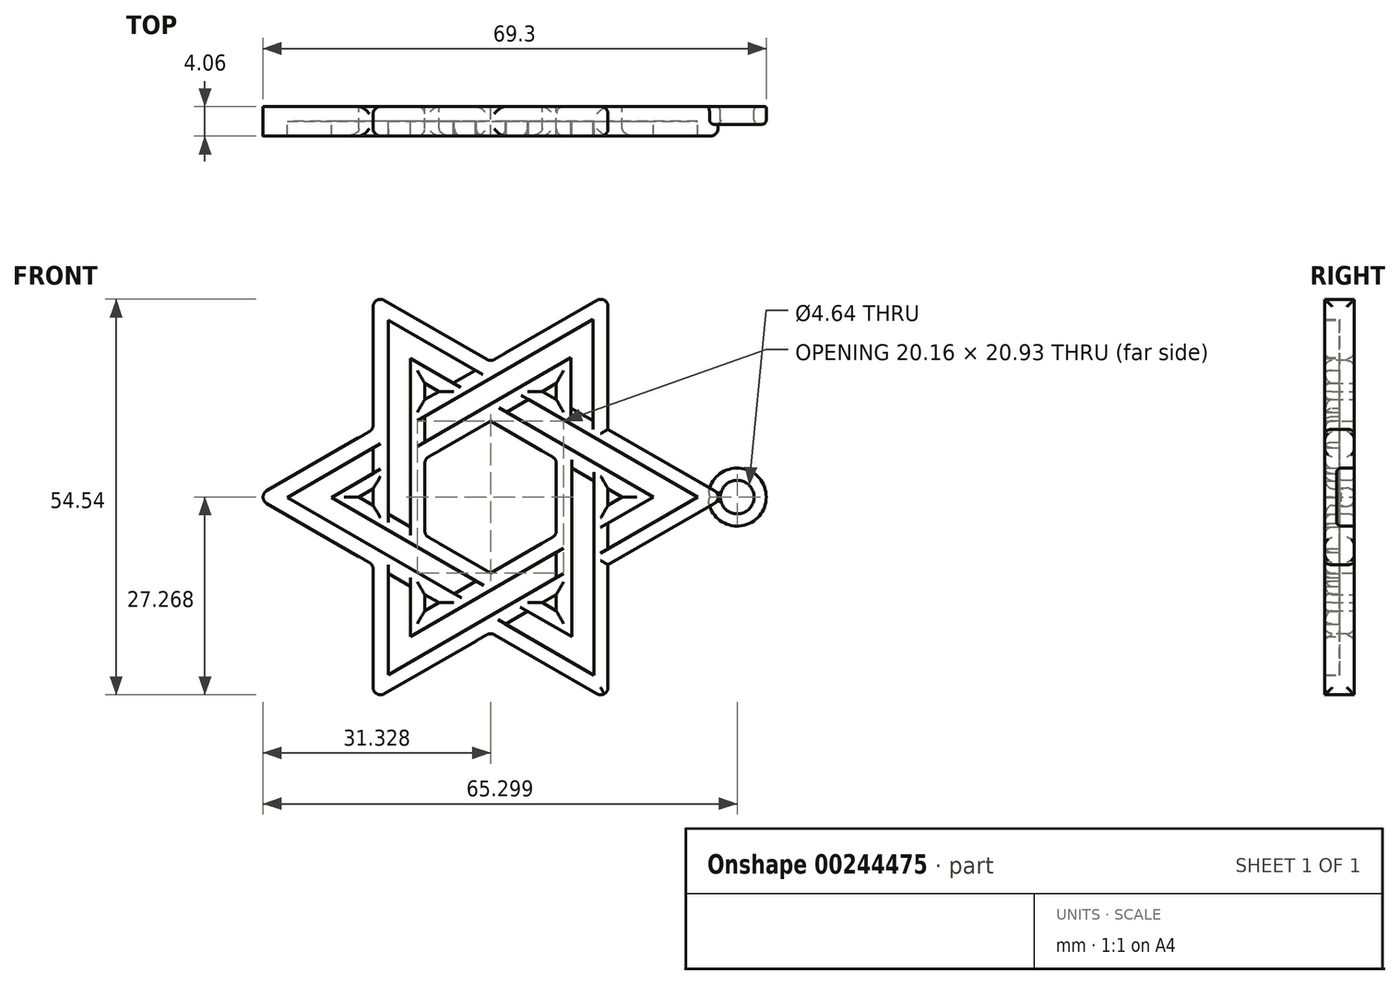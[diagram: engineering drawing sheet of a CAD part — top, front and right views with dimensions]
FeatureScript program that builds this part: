
annotation { "Feature Type Name" : "Feature", "Feature Type Description" : "" }
export const myFeature = defineFeature(function(context is Context, id is Id, definition is map)
    precondition{}
    {
        {
            var Q0;
            Q0=qCreatedBy(makeId("Front.planeOp"),FACE);
            var sketch = newSketch(context, id + "F0", { "sketchPlane" : qUnion([Q0])});
            skLineSegment(sketch, "E0.0", {"start": v(-25.14, 72.22) * mm, "end": v(-25.14, 48.87) * mm});
            skLineSegment(sketch, "E0.1", {"start": v(-25.14, 2.18) * mm, "end": v(-45.36, 13.85) * mm});
            skLineSegment(sketch, "E0.2", {"start": v(-85.8, 37.2) * mm, "end": v(-65.58, 48.87) * mm});
            skPoint(sketch, "E0.0.midPoint", {"position": v(-25.14, 37.2) * mm});
            skCircle(sketch, "E1.cCircle", {"center": v(-45.36, 37.2) * mm, "radius": 20.22 * mm, "construction": true});
            skLineSegment(sketch, "E1.0", {"start": v(-65.58, 2.18) * mm, "end": v(-65.58, 25.53) * mm});
            skLineSegment(sketch, "E1.1", {"start": v(-65.58, 72.22) * mm, "end": v(-45.36, 60.54) * mm});
            skLineSegment(sketch, "E1.2", {"start": v(-4.93, 37.2) * mm, "end": v(-25.14, 25.53) * mm});
            skPoint(sketch, "E1.0.midPoint", {"position": v(-65.58, 37.2) * mm});
            skLineSegment(sketch, "E2", {"start": v(-36.47, 55.41) * mm, "end": v(-25.14, 48.87) * mm});
            skLineSegment(sketch, "E3", {"start": v(-45.36, 60.54) * mm, "end": v(-25.14, 72.22) * mm});
            skLineSegment(sketch, "E4", {"start": v(-25.14, 48.87) * mm, "end": v(-4.93, 37.2) * mm});
            skLineSegment(sketch, "E5", {"start": v(-25.14, 38.6) * mm, "end": v(-25.14, 25.53) * mm});
            skLineSegment(sketch, "E6", {"start": v(-25.14, 25.53) * mm, "end": v(-25.14, 2.18) * mm});
            skLineSegment(sketch, "E7", {"start": v(-34.03, 20.4) * mm, "end": v(-45.36, 13.85) * mm});
            skLineSegment(sketch, "E8", {"start": v(-45.36, 13.85) * mm, "end": v(-65.58, 2.18) * mm});
            skLineSegment(sketch, "E9", {"start": v(-54.25, 18.99) * mm, "end": v(-65.58, 25.53) * mm});
            skLineSegment(sketch, "E10", {"start": v(-65.58, 25.53) * mm, "end": v(-85.8, 37.2) * mm});
            skLineSegment(sketch, "E11", {"start": v(-65.58, 35.8) * mm, "end": v(-65.58, 48.87) * mm});
            skLineSegment(sketch, "E12", {"start": v(-65.58, 48.87) * mm, "end": v(-65.58, 72.22) * mm});
            skLineSegment(sketch, "E13", {"start": v(-56.69, 54) * mm, "end": v(-45.36, 60.54) * mm});
            skLineSegment(sketch, "E14.0", {"start": v(-56.69, 30.66) * mm, "end": v(-56.69, 43.74) * mm});
            skLineSegment(sketch, "E14.1", {"start": v(-45.36, 50.28) * mm, "end": v(-34.03, 43.74) * mm});
            skLineSegment(sketch, "E14.2", {"start": v(-34.03, 43.74) * mm, "end": v(-34.03, 30.66) * mm});
            skLineSegment(sketch, "E14.3", {"start": v(-56.69, 43.74) * mm, "end": v(-45.36, 50.28) * mm});
            skLineSegment(sketch, "E14.4", {"start": v(-34.03, 30.66) * mm, "end": v(-45.36, 24.12) * mm});
            skLineSegment(sketch, "E14.5", {"start": v(-45.36, 24.12) * mm, "end": v(-56.69, 30.66) * mm});
            skLineSegment(sketch, "E15", {"start": v(-54.2, 55.38) * mm, "end": v(-56.69, 56.82) * mm});
            skLineSegment(sketch, "E16", {"start": v(-56.69, 43.74) * mm, "end": v(-56.69, 56.82) * mm});
            skLineSegment(sketch, "E17", {"start": v(-34.03, 43.74) * mm, "end": v(-22.7, 37.2) * mm});
            skLineSegment(sketch, "E18", {"start": v(-25.2, 35.76) * mm, "end": v(-22.7, 37.2) * mm});
            skLineSegment(sketch, "E19", {"start": v(-65.53, 38.64) * mm, "end": v(-68.01, 37.2) * mm});
            skLineSegment(sketch, "E20", {"start": v(-56.69, 30.66) * mm, "end": v(-68.01, 37.2) * mm});
            skLineSegment(sketch, "E21", {"start": v(-56.69, 20.45) * mm, "end": v(-56.69, 17.58) * mm});
            skLineSegment(sketch, "E22", {"start": v(-45.36, 24.12) * mm, "end": v(-56.69, 17.58) * mm});
            skLineSegment(sketch, "E23", {"start": v(-36.52, 19.02) * mm, "end": v(-34.03, 17.58) * mm});
            skLineSegment(sketch, "E24", {"start": v(-34.03, 30.66) * mm, "end": v(-34.03, 17.58) * mm});
            skLineSegment(sketch, "E25", {"start": v(-45.36, 50.28) * mm, "end": v(-34.03, 56.82) * mm});
            skLineSegment(sketch, "E26", {"start": v(-34.03, 53.94) * mm, "end": v(-34.03, 56.82) * mm});
            skPoint(sketch, "E27.orphan", {"position": v(-30.1, 59.09) * mm});
            skPoint(sketch, "E28.orphan", {"position": v(-60.62, 59.09) * mm});
            skLineSegment(sketch, "E29.0", {"start": v(-44.1, 58.34) * mm, "end": v(-27.68, 67.82) * mm});
            skLineSegment(sketch, "E29.1", {"start": v(-56.69, 51.07) * mm, "end": v(-44.1, 58.34) * mm});
            skLineSegment(sketch, "E30.0", {"start": v(-46.63, 52.48) * mm, "end": v(-31.5, 61.22) * mm});
            skLineSegment(sketch, "E31.0", {"start": v(-31.5, 52.54) * mm, "end": v(-31.5, 61.22) * mm});
            skLineSegment(sketch, "E32.trimOffspring", {"start": v(-27.68, 67.82) * mm, "end": v(-27.68, 50.34) * mm});
            skLineSegment(sketch, "E33.trimOffspring", {"start": v(-54.15, 55.4) * mm, "end": v(-54.15, 55.47) * mm});
            skLineSegment(sketch, "E34.trimOffspring", {"start": v(-56.69, 46.67) * mm, "end": v(-46.63, 52.48) * mm});
            skLineSegment(sketch, "E35.0", {"start": v(-46.57, 16.05) * mm, "end": v(-62.98, 6.58) * mm});
            skLineSegment(sketch, "E35.1", {"start": v(-34.03, 23.29) * mm, "end": v(-46.57, 16.05) * mm});
            skLineSegment(sketch, "E36.0", {"start": v(-44.03, 21.92) * mm, "end": v(-59.17, 13.18) * mm});
            skLineSegment(sketch, "E37.0", {"start": v(-59.17, 21.83) * mm, "end": v(-59.17, 13.18) * mm});
            skLineSegment(sketch, "E38.trimOffspring", {"start": v(-62.98, 6.58) * mm, "end": v(-62.98, 24.03) * mm});
            skLineSegment(sketch, "E39.trimOffspring", {"start": v(-34.03, 27.69) * mm, "end": v(-44.03, 21.92) * mm});
            skLineSegment(sketch, "E40.0", {"start": v(-27.55, 25.45) * mm, "end": v(-27.55, 6.5) * mm});
            skLineSegment(sketch, "E41.0", {"start": v(-31.36, 30.59) * mm, "end": v(-31.36, 13.1) * mm});
            skLineSegment(sketch, "E42.0", {"start": v(-39, 17.52) * mm, "end": v(-31.36, 13.1) * mm});
            skLineSegment(sketch, "E43.trimOffspring", {"start": v(-27.55, 6.5) * mm, "end": v(-42.81, 15.32) * mm});
            skLineSegment(sketch, "E44.trimOffspring", {"start": v(-31.36, 42.2) * mm, "end": v(-31.36, 30.59) * mm});
            skLineSegment(sketch, "E45.0", {"start": v(-62.93, 48.75) * mm, "end": v(-62.93, 67.7) * mm});
            skLineSegment(sketch, "E45.1", {"start": v(-62.93, 34.26) * mm, "end": v(-62.93, 48.75) * mm});
            skLineSegment(sketch, "E46.0", {"start": v(-59.12, 43.62) * mm, "end": v(-59.12, 61.1) * mm});
            skLineSegment(sketch, "E47.0", {"start": v(-51.76, 56.85) * mm, "end": v(-59.12, 61.1) * mm});
            skLineSegment(sketch, "E48.trimOffspring", {"start": v(-62.93, 67.7) * mm, "end": v(-47.95, 59.05) * mm});
            skLineSegment(sketch, "E49.trimOffspring", {"start": v(-59.12, 32.06) * mm, "end": v(-59.12, 43.62) * mm});
            skLineSegment(sketch, "E50", {"start": v(-27.55, 25.45) * mm, "end": v(-27.55, 40) * mm});
            skLineSegment(sketch, "E51.0", {"start": v(-63.96, 27.67) * mm, "end": v(-80.37, 37.15) * mm});
            skLineSegment(sketch, "E52.0", {"start": v(-57.6, 28.4) * mm, "end": v(-72.75, 37.15) * mm});
            skLineSegment(sketch, "E53.0", {"start": v(-65.58, 41.28) * mm, "end": v(-72.75, 37.15) * mm});
            skLineSegment(sketch, "E54.trimOffspring", {"start": v(-80.37, 37.15) * mm, "end": v(-65.58, 45.68) * mm});
            skLineSegment(sketch, "E55.trimOffspring", {"start": v(-47.77, 22.73) * mm, "end": v(-57.6, 28.4) * mm});
            skLineSegment(sketch, "E56.0", {"start": v(-26.1, 46.67) * mm, "end": v(-9.68, 37.2) * mm});
            skLineSegment(sketch, "E56.1", {"start": v(-38.85, 54.04) * mm, "end": v(-26.1, 46.67) * mm});
            skLineSegment(sketch, "E57.0", {"start": v(-32.44, 45.94) * mm, "end": v(-17.3, 37.2) * mm});
            skLineSegment(sketch, "E58.0", {"start": v(-25.14, 32.67) * mm, "end": v(-17.3, 37.2) * mm});
            skLineSegment(sketch, "E59.trimOffspring", {"start": v(-9.68, 37.2) * mm, "end": v(-25.14, 28.27) * mm});
            skLineSegment(sketch, "E60.trimOffspring", {"start": v(-42.66, 51.84) * mm, "end": v(-32.44, 45.94) * mm});
            skLineSegment(sketch, "E61", {"start": v(-63.96, 27.67) * mm, "end": v(-51.58, 20.53) * mm});
            skSolve(sketch);
        }
        {
            var Q0;
            Q0 = qSketchRegion(id + "F0", true);
            var Q1;
            {var subQ7=sQuery(id+"F0.wireOp",EDGE,"E14.1");Q1=makeQuery(id+"F0.imprint","IMPRINT",FACE,{"disambiguationData":[TD([[makeQuery(id+"F0.imprint","IMPRINT",EDGE,{"derivedFrom":subQ7}),1.0]])]});}
            var Q2;
            {var subQ10=sQuery(id+"F0.wireOp",EDGE,"E14.3");Q2=makeQuery(id+"F0.imprint","IMPRINT",FACE,{"disambiguationData":[TD([[makeQuery(id+"F0.imprint","IMPRINT",EDGE,{"derivedFrom":subQ10}),1.0]])]});}
            var Q3;
            {var subQ9=sQuery(id+"F0.wireOp",EDGE,"E14.2");Q3=makeQuery(id+"F0.imprint","IMPRINT",FACE,{"disambiguationData":[TD([[makeQuery(id+"F0.imprint","IMPRINT",EDGE,{"derivedFrom":subQ9}),1.0]])]});}
            var Q4;
            {var subQ10=sQuery(id+"F0.wireOp",EDGE,"E14.4");Q4=makeQuery(id+"F0.imprint","IMPRINT",FACE,{"disambiguationData":[TD([[makeQuery(id+"F0.imprint","IMPRINT",EDGE,{"derivedFrom":subQ10}),1.0]])]});}
            var Q5;
            {var subQ7=sQuery(id+"F0.wireOp",EDGE,"E14.5");Q5=makeQuery(id+"F0.imprint","IMPRINT",FACE,{"disambiguationData":[TD([[makeQuery(id+"F0.imprint","IMPRINT",EDGE,{"derivedFrom":subQ7}),1.0]])]});}
            var Q6;
            {var subQ7=sQuery(id+"F0.wireOp",EDGE,"E14.0");Q6=makeQuery(id+"F0.imprint","IMPRINT",FACE,{"disambiguationData":[TD([[makeQuery(id+"F0.imprint","IMPRINT",EDGE,{"derivedFrom":subQ7}),1.0]])]});}
            extrude(context, id + "F1", {"entities" : qUnion([Q0, Q1, Q2, Q3, Q4, Q5, Q6]), "depth" : 5.08 * mm});
        }
        {
            var Q0;
            Q0=makeQuery(id+"F0.imprint","IMPRINT",FACE,{"disambiguationData":[TD([[makeQuery(id+"F0.imprint","IMPRINT",EDGE,{"derivedFrom":sQuery(id+"F0.wireOp",EDGE,"E45.0")}),-1.0]])]});
            var Q1;
            Q1=makeQuery(id+"F0.imprint","IMPRINT",FACE,{"disambiguationData":[TD([[makeQuery(id+"F0.imprint","IMPRINT",EDGE,{"derivedFrom":sQuery(id+"F0.wireOp",EDGE,"E29.0")}),-1.0]])]});
            var Q2;
            Q2=makeQuery(id+"F0.imprint","IMPRINT",FACE,{"disambiguationData":[TD([[makeQuery(id+"F0.imprint","IMPRINT",EDGE,{"derivedFrom":sQuery(id+"F0.wireOp",EDGE,"E56.0")}),-1.0]])]});
            var Q3;
            Q3=makeQuery(id+"F0.imprint","IMPRINT",FACE,{"disambiguationData":[TD([[makeQuery(id+"F0.imprint","IMPRINT",EDGE,{"derivedFrom":sQuery(id+"F0.wireOp",EDGE,"E40.0")}),-1.0]])]});
            var Q4;
            Q4=makeQuery(id+"F0.imprint","IMPRINT",FACE,{"disambiguationData":[TD([[makeQuery(id+"F0.imprint","IMPRINT",EDGE,{"derivedFrom":sQuery(id+"F0.wireOp",EDGE,"E35.0")}),-1.0]])]});
            var Q5;
            Q5=makeQuery(id+"F0.imprint","IMPRINT",FACE,{"disambiguationData":[TD([[makeQuery(id+"F0.imprint","IMPRINT",EDGE,{"derivedFrom":sQuery(id+"F0.wireOp",EDGE,"E51.0")}),-1.0]])]});
            extrude(context, id + "F2", {"entities" : qUnion([Q0, Q1, Q2, Q3, Q4, Q5]), "operationType" : NewBodyOperationType.ADD, "depth" : 2.54 * mm});
        }
        {
            var Q0;
            {var subQ0=sQuery(id+"F0.wireOp",EDGE,"3791ea46-a5e9-4ab1-a861-55320faec565.trimOffspring");var subQ1=sQuery(id+"F0.wireOp",EDGE,"E60.trimOffspring");var subQ2=sQuery(id+"F0.wireOp",EDGE,"E59.trimOffspring");var subQ3=sQuery(id+"F0.wireOp",EDGE,"b85427f2-48fe-4ba3-bfe0-d898cf596bcf.0");var subQ4=sQuery(id+"F0.wireOp",EDGE,"E58.0");var subQ5=sQuery(id+"F0.wireOp",EDGE,"E57.0");var subQ6=sQuery(id+"F0.wireOp",EDGE,"E56.1");var subQ7=sQuery(id+"F0.wireOp",EDGE,"E56.0");var subQ8=sQuery(id+"F0.wireOp",EDGE,"E61");var subQ9=sQuery(id+"F0.wireOp",EDGE,"51e37403-e772-4eac-ae45-40e6eff04354.trimOffspring");var subQ10=sQuery(id+"F0.wireOp",EDGE,"E55.trimOffspring");var subQ11=sQuery(id+"F0.wireOp",EDGE,"E54.trimOffspring");var subQ12=sQuery(id+"F0.wireOp",EDGE,"bc42f384-2414-4325-8679-d2749f00dfbf.0");var subQ13=sQuery(id+"F0.wireOp",EDGE,"E53.0");var subQ14=sQuery(id+"F0.wireOp",EDGE,"E52.0");var subQ15=sQuery(id+"F0.wireOp",EDGE,"E51.0");var subQ16=sQuery(id+"F0.wireOp",EDGE,"242a467f-4fe9-4b40-a065-2ee8d1ec2a3d.trimOffspring");var subQ17=sQuery(id+"F0.wireOp",EDGE,"E49.trimOffspring");var subQ18=sQuery(id+"F0.wireOp",EDGE,"E48.trimOffspring");var subQ19=sQuery(id+"F0.wireOp",EDGE,"76f297ee-8d65-411f-9fbc-2a5ef9db8cba.0");var subQ20=sQuery(id+"F0.wireOp",EDGE,"E47.0");var subQ21=sQuery(id+"F0.wireOp",EDGE,"E46.0");var subQ22=sQuery(id+"F0.wireOp",EDGE,"E45.1");var subQ23=sQuery(id+"F0.wireOp",EDGE,"E45.0");var subQ24=sQuery(id+"F0.wireOp",EDGE,"E50");var subQ25=sQuery(id+"F0.wireOp",EDGE,"70ba2939-24bf-49fa-9c79-4e4c6b037132.trimOffspring");var subQ26=sQuery(id+"F0.wireOp",EDGE,"E44.trimOffspring");var subQ27=sQuery(id+"F0.wireOp",EDGE,"E43.trimOffspring");var subQ28=sQuery(id+"F0.wireOp",EDGE,"54159dc6-59ae-437a-bbb7-fb0cfa8d277d.0");var subQ29=sQuery(id+"F0.wireOp",EDGE,"E42.0");var subQ30=sQuery(id+"F0.wireOp",EDGE,"E41.0");var subQ31=sQuery(id+"F0.wireOp",EDGE,"E40.0");var subQ32=sQuery(id+"F0.wireOp",EDGE,"9e70e6bb-2b84-45bd-9e91-4ec9be9ea51e.trimOffspring");var subQ33=sQuery(id+"F0.wireOp",EDGE,"E39.trimOffspring");var subQ34=sQuery(id+"F0.wireOp",EDGE,"E38.trimOffspring");var subQ35=sQuery(id+"F0.wireOp",EDGE,"b6243921-ca12-479c-9c0a-cf2d943f5022.0");var subQ36=sQuery(id+"F0.wireOp",EDGE,"E37.0");var subQ37=sQuery(id+"F0.wireOp",EDGE,"E36.0");var subQ38=sQuery(id+"F0.wireOp",EDGE,"E35.1");var subQ39=sQuery(id+"F0.wireOp",EDGE,"E35.0");var subQ40=sQuery(id+"F0.wireOp",EDGE,"5713abb0-698d-4ae2-b673-d070041138cb.trimOffspring");var subQ41=sQuery(id+"F0.wireOp",EDGE,"E34.trimOffspring");var subQ42=sQuery(id+"F0.wireOp",EDGE,"E32.trimOffspring");var subQ43=sQuery(id+"F0.wireOp",EDGE,"0343537c-8046-475e-9b01-e672b3182352.0");var subQ44=sQuery(id+"F0.wireOp",EDGE,"E31.0");var subQ45=sQuery(id+"F0.wireOp",EDGE,"E30.0");var subQ46=sQuery(id+"F0.wireOp",EDGE,"E29.1");var subQ47=sQuery(id+"F0.wireOp",EDGE,"E29.0");Q0=makeQuery(id+"F2.boolean.opBoolean","MERGE",FACE,{"derivedFrom":[makeQuery(id+"F1.opExtrude","CAP_FACE",FACE,{"disambiguationData":[OSD([sQuery(id+"F0.wireOp",EDGE,"E0.0"),sQuery(id+"F0.wireOp",EDGE,"E0.1"),sQuery(id+"F0.wireOp",EDGE,"E0.2"),sQuery(id+"F0.wireOp",EDGE,"E1.0"),sQuery(id+"F0.wireOp",EDGE,"E1.1"),sQuery(id+"F0.wireOp",EDGE,"E1.2"),sQuery(id+"F0.wireOp",EDGE,"E2"),sQuery(id+"F0.wireOp",EDGE,"E3"),sQuery(id+"F0.wireOp",EDGE,"E4"),sQuery(id+"F0.wireOp",EDGE,"E5"),sQuery(id+"F0.wireOp",EDGE,"E6"),sQuery(id+"F0.wireOp",EDGE,"E7"),sQuery(id+"F0.wireOp",EDGE,"E8"),sQuery(id+"F0.wireOp",EDGE,"E9"),sQuery(id+"F0.wireOp",EDGE,"E10"),sQuery(id+"F0.wireOp",EDGE,"E11"),sQuery(id+"F0.wireOp",EDGE,"E12"),sQuery(id+"F0.wireOp",EDGE,"E13"),sQuery(id+"F0.wireOp",EDGE,"E14.0"),sQuery(id+"F0.wireOp",EDGE,"E14.1"),sQuery(id+"F0.wireOp",EDGE,"E14.2"),sQuery(id+"F0.wireOp",EDGE,"E14.3"),sQuery(id+"F0.wireOp",EDGE,"E14.4"),sQuery(id+"F0.wireOp",EDGE,"E14.5"),sQuery(id+"F0.wireOp",EDGE,"E15"),sQuery(id+"F0.wireOp",EDGE,"E16"),sQuery(id+"F0.wireOp",EDGE,"E17"),sQuery(id+"F0.wireOp",EDGE,"E18"),sQuery(id+"F0.wireOp",EDGE,"E19"),sQuery(id+"F0.wireOp",EDGE,"E20"),sQuery(id+"F0.wireOp",EDGE,"E21"),sQuery(id+"F0.wireOp",EDGE,"E22"),sQuery(id+"F0.wireOp",EDGE,"E23"),sQuery(id+"F0.wireOp",EDGE,"E24"),sQuery(id+"F0.wireOp",EDGE,"E25"),sQuery(id+"F0.wireOp",EDGE,"E26"),subQ47,subQ46,subQ45,subQ44,subQ43,subQ42,subQ41,subQ40,subQ39,subQ38,subQ37,subQ36,subQ35,subQ34,subQ33,subQ32,subQ31,subQ30,subQ29,subQ28,subQ27,subQ26,subQ25,subQ23,subQ22,subQ21,subQ20,subQ19,subQ18,subQ17,subQ16,subQ24,subQ15,subQ14,subQ13,subQ12,subQ11,subQ10,subQ9,subQ7,subQ6,subQ5,subQ4,subQ3,subQ2,subQ1,subQ0,subQ8])],"isStart":true}),makeQuery(id+"F2.opExtrude","CAP_FACE",FACE,{"disambiguationData":[OSD([subQ47,subQ46,subQ45,subQ44,subQ43,subQ42,subQ41,subQ40])],"isStart":true}),makeQuery(id+"F2.opExtrude","CAP_FACE",FACE,{"disambiguationData":[OSD([subQ39,subQ38,subQ37,subQ36,subQ35,subQ34,subQ33,subQ32])],"isStart":true}),makeQuery(id+"F2.opExtrude","CAP_FACE",FACE,{"disambiguationData":[OSD([subQ31,subQ30,subQ29,subQ28,subQ27,subQ26,subQ25,subQ24])],"isStart":true}),makeQuery(id+"F2.opExtrude","CAP_FACE",FACE,{"disambiguationData":[OSD([subQ23,subQ22,subQ21,subQ20,subQ19,subQ18,subQ17,subQ16])],"isStart":true}),makeQuery(id+"F2.opExtrude","CAP_FACE",FACE,{"disambiguationData":[OSD([subQ15,subQ14,subQ13,subQ12,subQ11,subQ10,subQ9,subQ8])],"isStart":true}),makeQuery(id+"F2.opExtrude","CAP_FACE",FACE,{"disambiguationData":[OSD([subQ7,subQ6,subQ5,subQ4,subQ3,subQ2,subQ1,subQ0])],"isStart":true})]});}
            var sketch = newSketch(context, id + "F3", { "sketchPlane" : qUnion([Q0])});
            skCircle(sketch, "E62", {"center": v(2.9, 37.2) * mm, "radius": 5 * mm});
            skCircle(sketch, "E63", {"center": v(2.9, 37.2) * mm, "radius": 2.9 * mm});
            skSolve(sketch);
        }
        {
            var Q0;
            Q0=makeQuery(id+"F1.opExtrude","SWEPT_FACE",FACE,{"disambiguationData":[OSD([sQuery(id+"F0.wireOp",EDGE,"E0.1")])]});
            var Q1;
            Q1=makeQuery(id+"F1.opExtrude","SWEPT_FACE",FACE,{"disambiguationData":[OSD([sQuery(id+"F0.wireOp",EDGE,"E1.0")])]});
            var Q2;
            Q2=makeQuery(id+"F1.opExtrude","SWEPT_FACE",FACE,{"disambiguationData":[OSD([sQuery(id+"F0.wireOp",EDGE,"E12")])]});
            var Q3;
            Q3=makeQuery(id+"F1.opExtrude","SWEPT_FACE",FACE,{"disambiguationData":[OSD([sQuery(id+"F0.wireOp",EDGE,"E1.1")])]});
            var Q4;
            Q4=makeQuery(id+"F1.opExtrude","SWEPT_FACE",FACE,{"disambiguationData":[OSD([sQuery(id+"F0.wireOp",EDGE,"E14.0")])]});
            var Q5;
            Q5=makeQuery(id+"F1.opExtrude","SWEPT_FACE",FACE,{"disambiguationData":[OSD([sQuery(id+"F0.wireOp",EDGE,"E14.2")])]});
            var Q6;
            Q6=makeQuery(id+"F1.opExtrude","SWEPT_EDGE",EDGE,{"disambiguationData":[OSD([sQuery(id+"F0.wireOp",EDGE,"E0.0"),sQuery(id+"F0.wireOp",EDGE,"E3")])]});
            var Q7;
            Q7=makeQuery(id+"F1.opExtrude","CAP_EDGE",EDGE,{"disambiguationData":[OSD([sQuery(id+"F0.wireOp",EDGE,"E18")])],"isStart":false});
            var Q8;
            Q8=makeQuery(id+"F1.opExtrude","CAP_EDGE",EDGE,{"disambiguationData":[OSD([sQuery(id+"F0.wireOp",EDGE,"E17")])],"isStart":false});
            var Q9;
            Q9=makeQuery(id+"F1.opExtrude","CAP_EDGE",EDGE,{"disambiguationData":[OSD([sQuery(id+"F0.wireOp",EDGE,"E5")])],"isStart":false});
            var Q10;
            Q10=makeQuery(id+"F1.opExtrude","CAP_EDGE",EDGE,{"disambiguationData":[OSD([sQuery(id+"F0.wireOp",EDGE,"E24")])],"isStart":false});
            var Q11;
            Q11=makeQuery(id+"F1.opExtrude","CAP_EDGE",EDGE,{"disambiguationData":[OSD([sQuery(id+"F0.wireOp",EDGE,"E23")])],"isStart":false});
            var Q12;
            Q12=makeQuery(id+"F1.opExtrude","CAP_EDGE",EDGE,{"disambiguationData":[OSD([sQuery(id+"F0.wireOp",EDGE,"E7")])],"isStart":false});
            var Q13;
            Q13=makeQuery(id+"F1.opExtrude","CAP_EDGE",EDGE,{"disambiguationData":[OSD([sQuery(id+"F0.wireOp",EDGE,"E26")])],"isStart":false});
            var Q14;
            Q14=makeQuery(id+"F1.opExtrude","CAP_EDGE",EDGE,{"disambiguationData":[OSD([sQuery(id+"F0.wireOp",EDGE,"E2")])],"isStart":false});
            var Q15;
            Q15=makeQuery(id+"F1.opExtrude","CAP_EDGE",EDGE,{"disambiguationData":[OSD([sQuery(id+"F0.wireOp",EDGE,"E25")])],"isStart":false});
            var Q16;
            Q16=makeQuery(id+"F1.opExtrude","CAP_EDGE",EDGE,{"disambiguationData":[OSD([sQuery(id+"F0.wireOp",EDGE,"E16")])],"isStart":false});
            var Q17;
            Q17=makeQuery(id+"F1.opExtrude","CAP_EDGE",EDGE,{"disambiguationData":[OSD([sQuery(id+"F0.wireOp",EDGE,"E15")])],"isStart":false});
            var Q18;
            Q18=makeQuery(id+"F1.opExtrude","CAP_EDGE",EDGE,{"disambiguationData":[OSD([sQuery(id+"F0.wireOp",EDGE,"E13")])],"isStart":false});
            var Q19;
            Q19=makeQuery(id+"F1.opExtrude","CAP_EDGE",EDGE,{"disambiguationData":[OSD([sQuery(id+"F0.wireOp",EDGE,"E22")])],"isStart":false});
            var Q20;
            Q20=makeQuery(id+"F1.opExtrude","CAP_EDGE",EDGE,{"disambiguationData":[OSD([sQuery(id+"F0.wireOp",EDGE,"E9")])],"isStart":false});
            var Q21;
            Q21=makeQuery(id+"F1.opExtrude","CAP_EDGE",EDGE,{"disambiguationData":[OSD([sQuery(id+"F0.wireOp",EDGE,"E21")])],"isStart":false});
            var Q22;
            Q22=makeQuery(id+"F1.opExtrude","CAP_EDGE",EDGE,{"disambiguationData":[OSD([sQuery(id+"F0.wireOp",EDGE,"E11")])],"isStart":false});
            var Q23;
            Q23=makeQuery(id+"F1.opExtrude","CAP_EDGE",EDGE,{"disambiguationData":[OSD([sQuery(id+"F0.wireOp",EDGE,"E20")])],"isStart":false});
            var Q24;
            Q24=makeQuery(id+"F1.opExtrude","CAP_EDGE",EDGE,{"disambiguationData":[OSD([sQuery(id+"F0.wireOp",EDGE,"E19")])],"isStart":false});
            var Q25;
            Q25=makeQuery(id+"F1.opExtrude","SWEPT_EDGE",EDGE,{"disambiguationData":[OSD([sQuery(id+"F0.wireOp",EDGE,"E0.2"),sQuery(id+"F0.wireOp",EDGE,"E10")])]});
            fillet(context, id + "F4", {"entities" : qUnion([Q0, Q1, Q2, Q3, Q4, Q5, Q6, Q7, Q8, Q9, Q10, Q11, Q12, Q13, Q14, Q15, Q16, Q17, Q18, Q19, Q20, Q21, Q22, Q23, Q24, Q25]), "radius" : 1.27 * mm, "tangentPropagation" : true, "allowEdgeOverflow" : false});
        }
        {
            var Q0;
            Q0=makeQuery(id+"F1.opExtrude","CAP_EDGE",EDGE,{"disambiguationData":[OSD([sQuery(id+"F0.wireOp",EDGE,"E0.0")])],"isStart":false});
            var Q1;
            Q1=makeQuery(id+"F1.opExtrude","CAP_EDGE",EDGE,{"disambiguationData":[OSD([sQuery(id+"F0.wireOp",EDGE,"E0.0")])],"isStart":true});
            var Q2;
            Q2=makeQuery(id+"F1.opExtrude","CAP_EDGE",EDGE,{"disambiguationData":[OSD([sQuery(id+"F0.wireOp",EDGE,"E4")])],"isStart":false});
            var Q3;
            Q3=makeQuery(id+"F1.opExtrude","CAP_EDGE",EDGE,{"disambiguationData":[OSD([sQuery(id+"F0.wireOp",EDGE,"E1.2")])],"isStart":false});
            var Q4;
            Q4=makeQuery(id+"F1.opExtrude","CAP_EDGE",EDGE,{"disambiguationData":[OSD([sQuery(id+"F0.wireOp",EDGE,"E6")])],"isStart":false});
            var Q5;
            Q5=makeQuery(id+"F1.opExtrude","CAP_EDGE",EDGE,{"disambiguationData":[OSD([sQuery(id+"F0.wireOp",EDGE,"E6")])],"isStart":true});
            var Q6;
            {var subQ18=sQuery(id+"F0.wireOp",EDGE,"E1.2");var subQ51=sQuery(id+"F0.wireOp",EDGE,"E6");Q6=makeQuery(id+"FdHpB2eBTlVxnf4_1.boolean.opBoolean","SPLIT",EDGE,{"disambiguationData":[TD([makeQuery(id+"F1.opExtrude","SWEPT_FACE",FACE,{"disambiguationData":[OSD([subQ51])]})])],"derivedFrom":makeQuery(id+"F1.opExtrude","CAP_EDGE",EDGE,{"disambiguationData":[OSD([subQ18])],"isStart":true})});}
            var Q7;
            {var subQ17=sQuery(id+"F0.wireOp",EDGE,"E4");var subQ51=sQuery(id+"F0.wireOp",EDGE,"E0.0");Q7=makeQuery(id+"FdHpB2eBTlVxnf4_1.boolean.opBoolean","SPLIT",EDGE,{"disambiguationData":[TD([makeQuery(id+"F1.opExtrude","SWEPT_FACE",FACE,{"disambiguationData":[OSD([subQ51])]})])],"derivedFrom":makeQuery(id+"F1.opExtrude","CAP_EDGE",EDGE,{"disambiguationData":[OSD([subQ17])],"isStart":true})});}
            var Q8;
            Q8=makeQuery(id+"F1.opExtrude","SWEPT_EDGE",EDGE,{"disambiguationData":[OSD([sQuery(id+"F0.wireOp",EDGE,"E1.2"),sQuery(id+"F0.wireOp",EDGE,"E4")])]});
            fillet(context, id + "F5", {"entities" : qUnion([Q0, Q1, Q2, Q3, Q4, Q5, Q6, Q7, Q8]), "radius" : 1.27 * mm, "allowEdgeOverflow" : false});
        }
        {
            var Q0;
            Q0=makeQuery(id+"F2.opExtrude","CAP_FACE",FACE,{"disambiguationData":[OSD([sQuery(id+"F0.wireOp",EDGE,"E29.0"),sQuery(id+"F0.wireOp",EDGE,"E29.1"),sQuery(id+"F0.wireOp",EDGE,"E30.0"),sQuery(id+"F0.wireOp",EDGE,"E31.0"),sQuery(id+"F0.wireOp",EDGE,"0343537c-8046-475e-9b01-e672b3182352.0"),sQuery(id+"F0.wireOp",EDGE,"E32.trimOffspring"),sQuery(id+"F0.wireOp",EDGE,"E34.trimOffspring"),sQuery(id+"F0.wireOp",EDGE,"5713abb0-698d-4ae2-b673-d070041138cb.trimOffspring")])],"isStart":false});
            var sketch = newSketch(context, id + "F6", { "sketchPlane" : qUnion([Q0])});
            skSolve(sketch);
        }
        {
            var Q0;
            Q0=makeQuery(id+"F6.imprint","IMPRINT",FACE,{"disambiguationData":[TD([[makeQuery(id+"F6.imprint","IMPRINT",EDGE,{"derivedFrom":makeQuery(id+"F2.opExtrude","CAP_EDGE",EDGE,{"disambiguationData":[OSD([sQuery(id+"F0.wireOp",EDGE,"E31.0")])],"isStart":false})}),-1.0]])]});
            var Q1;
            Q1=makeQuery(id+"F2.opExtrude","CAP_FACE",FACE,{"disambiguationData":[OSD([sQuery(id+"F0.wireOp",EDGE,"E40.0"),sQuery(id+"F0.wireOp",EDGE,"E41.0"),sQuery(id+"F0.wireOp",EDGE,"E42.0"),sQuery(id+"F0.wireOp",EDGE,"54159dc6-59ae-437a-bbb7-fb0cfa8d277d.0"),sQuery(id+"F0.wireOp",EDGE,"E43.trimOffspring"),sQuery(id+"F0.wireOp",EDGE,"E44.trimOffspring"),sQuery(id+"F0.wireOp",EDGE,"70ba2939-24bf-49fa-9c79-4e4c6b037132.trimOffspring"),sQuery(id+"F0.wireOp",EDGE,"E50")])],"isStart":false});
            var Q2;
            Q2=makeQuery(id+"F2.opExtrude","CAP_FACE",FACE,{"disambiguationData":[OSD([sQuery(id+"F0.wireOp",EDGE,"E56.0"),sQuery(id+"F0.wireOp",EDGE,"E56.1"),sQuery(id+"F0.wireOp",EDGE,"E57.0"),sQuery(id+"F0.wireOp",EDGE,"E58.0"),sQuery(id+"F0.wireOp",EDGE,"b85427f2-48fe-4ba3-bfe0-d898cf596bcf.0"),sQuery(id+"F0.wireOp",EDGE,"E59.trimOffspring"),sQuery(id+"F0.wireOp",EDGE,"E60.trimOffspring"),sQuery(id+"F0.wireOp",EDGE,"3791ea46-a5e9-4ab1-a861-55320faec565.trimOffspring")])],"isStart":false});
            var Q3;
            Q3=makeQuery(id+"F2.opExtrude","CAP_FACE",FACE,{"disambiguationData":[OSD([sQuery(id+"F0.wireOp",EDGE,"E35.0"),sQuery(id+"F0.wireOp",EDGE,"E35.1"),sQuery(id+"F0.wireOp",EDGE,"E36.0"),sQuery(id+"F0.wireOp",EDGE,"E37.0"),sQuery(id+"F0.wireOp",EDGE,"b6243921-ca12-479c-9c0a-cf2d943f5022.0"),sQuery(id+"F0.wireOp",EDGE,"E38.trimOffspring"),sQuery(id+"F0.wireOp",EDGE,"E39.trimOffspring"),sQuery(id+"F0.wireOp",EDGE,"9e70e6bb-2b84-45bd-9e91-4ec9be9ea51e.trimOffspring")])],"isStart":false});
            var Q4;
            Q4=makeQuery(id+"F2.opExtrude","CAP_FACE",FACE,{"disambiguationData":[OSD([sQuery(id+"F0.wireOp",EDGE,"E51.0"),sQuery(id+"F0.wireOp",EDGE,"E52.0"),sQuery(id+"F0.wireOp",EDGE,"E53.0"),sQuery(id+"F0.wireOp",EDGE,"bc42f384-2414-4325-8679-d2749f00dfbf.0"),sQuery(id+"F0.wireOp",EDGE,"E54.trimOffspring"),sQuery(id+"F0.wireOp",EDGE,"E55.trimOffspring"),sQuery(id+"F0.wireOp",EDGE,"51e37403-e772-4eac-ae45-40e6eff04354.trimOffspring"),sQuery(id+"F0.wireOp",EDGE,"E61")])],"isStart":false});
            var Q5;
            Q5=makeQuery(id+"F2.opExtrude","CAP_FACE",FACE,{"disambiguationData":[OSD([sQuery(id+"F0.wireOp",EDGE,"E45.0"),sQuery(id+"F0.wireOp",EDGE,"E45.1"),sQuery(id+"F0.wireOp",EDGE,"E46.0"),sQuery(id+"F0.wireOp",EDGE,"E47.0"),sQuery(id+"F0.wireOp",EDGE,"76f297ee-8d65-411f-9fbc-2a5ef9db8cba.0"),sQuery(id+"F0.wireOp",EDGE,"E48.trimOffspring"),sQuery(id+"F0.wireOp",EDGE,"E49.trimOffspring"),sQuery(id+"F0.wireOp",EDGE,"242a467f-4fe9-4b40-a065-2ee8d1ec2a3d.trimOffspring")])],"isStart":false});
            extrude(context, id + "F7", {"entities" : qUnion([Q0, Q1, Q2, Q3, Q4, Q5]), "depth" : 2.54 * mm});
        }
        {
            var Q0;
            {var subQ0=sQuery(id+"F3.wireOp",EDGE,"E62");var subQ1=makeQuery(id+"F1.opExtrude","CAP_EDGE",EDGE,{"disambiguationData":[OSD([sQuery(id+"F0.wireOp",EDGE,"E1.2")])],"isStart":true});var subQ2=makeQuery(id+"F3.imprint","INTERSECT",VERTEX,{"derivedFrom":[subQ1,subQ0]});Q0=makeQuery(id+"F3.imprint","IMPRINT",FACE,{"disambiguationData":[TD([[makeQuery(id+"F3.imprint","IMPRINT",EDGE,{"disambiguationData":[TD([[subQ2,1.0]])],"derivedFrom":subQ0}),1.0]])]});}
            var Q1;
            {var subQ0=sQuery(id+"F3.wireOp",EDGE,"E62");var subQ1=makeQuery(id+"F1.opExtrude","CAP_EDGE",EDGE,{"disambiguationData":[OSD([sQuery(id+"F0.wireOp",EDGE,"E1.2")])],"isStart":true});var subQ2=makeQuery(id+"F3.imprint","INTERSECT",VERTEX,{"derivedFrom":[subQ1,subQ0]});Q1=makeQuery(id+"F3.imprint","IMPRINT",FACE,{"disambiguationData":[TD([[makeQuery(id+"F3.imprint","IMPRINT",EDGE,{"disambiguationData":[TD([[subQ2,-1.0]])],"derivedFrom":subQ0}),1.0]])]});}
            extrude(context, id + "F8", {"entities" : qUnion([Q0, Q1]), "operationType" : NewBodyOperationType.ADD, "oppositeDirection" : true, "depth" : 3.05 * mm});
        }
        {
            var Q0;
            Q0=makeQuery(id+"F8.opExtrude","SWEPT_FACE",FACE,{"disambiguationData":[OSD([sQuery(id+"F3.wireOp",EDGE,"E63")])]});
            var Q1;
            Q1=makeQuery(id+"F8.opExtrude","CAP_EDGE",EDGE,{"disambiguationData":[OSD([sQuery(id+"F3.wireOp",EDGE,"E62")])],"isStart":false});
            fillet(context, id + "F9", {"entities" : qUnion([Q0, Q1]), "radius" : 0.76 * mm, "tangentPropagation" : true, "allowEdgeOverflow" : false});
        }
        {
            var Q0;
            Q0=makeQuery(id+"F8.opExtrude","CAP_EDGE",EDGE,{"disambiguationData":[OSD([sQuery(id+"F3.wireOp",EDGE,"E62")])],"isStart":true});
            fillet(context, id + "F10", {"entities" : qUnion([Q0]), "radius" : 0.25 * mm, "tangentPropagation" : true, "allowEdgeOverflow" : false});
        }
        {
            var Q0;
            Q0=makeQuery(id+"F7.opExtrude","SWEPT_BODY",BODY,{"disambiguationData":[OSD([sQuery(id+"F0.wireOp",EDGE,"E2"),sQuery(id+"F0.wireOp",EDGE,"E16"),sQuery(id+"F0.wireOp",EDGE,"E29.0"),sQuery(id+"F0.wireOp",EDGE,"E29.1"),sQuery(id+"F0.wireOp",EDGE,"E30.0"),sQuery(id+"F0.wireOp",EDGE,"E31.0"),sQuery(id+"F0.wireOp",EDGE,"E32.trimOffspring"),sQuery(id+"F0.wireOp",EDGE,"E34.trimOffspring")])]});
            var Q1;
            Q1=makeQuery(id+"F7.opExtrude","SWEPT_BODY",BODY,{"disambiguationData":[OSD([sQuery(id+"F0.wireOp",EDGE,"E13"),sQuery(id+"F0.wireOp",EDGE,"E20"),sQuery(id+"F0.wireOp",EDGE,"E45.0"),sQuery(id+"F0.wireOp",EDGE,"E45.1"),sQuery(id+"F0.wireOp",EDGE,"E46.0"),sQuery(id+"F0.wireOp",EDGE,"E47.0"),sQuery(id+"F0.wireOp",EDGE,"E48.trimOffspring"),sQuery(id+"F0.wireOp",EDGE,"E49.trimOffspring")])]});
            var Q2;
            Q2=makeQuery(id+"F7.opExtrude","SWEPT_BODY",BODY,{"disambiguationData":[OSD([sQuery(id+"F0.wireOp",EDGE,"E11"),sQuery(id+"F0.wireOp",EDGE,"E22"),sQuery(id+"F0.wireOp",EDGE,"E51.0"),sQuery(id+"F0.wireOp",EDGE,"E52.0"),sQuery(id+"F0.wireOp",EDGE,"E53.0"),sQuery(id+"F0.wireOp",EDGE,"E54.trimOffspring"),sQuery(id+"F0.wireOp",EDGE,"E55.trimOffspring"),sQuery(id+"F0.wireOp",EDGE,"E61")])]});
            var Q3;
            Q3=makeQuery(id+"F7.opExtrude","SWEPT_BODY",BODY,{"disambiguationData":[OSD([sQuery(id+"F0.wireOp",EDGE,"E9"),sQuery(id+"F0.wireOp",EDGE,"E24"),sQuery(id+"F0.wireOp",EDGE,"E35.0"),sQuery(id+"F0.wireOp",EDGE,"E35.1"),sQuery(id+"F0.wireOp",EDGE,"E36.0"),sQuery(id+"F0.wireOp",EDGE,"E37.0"),sQuery(id+"F0.wireOp",EDGE,"E38.trimOffspring"),sQuery(id+"F0.wireOp",EDGE,"E39.trimOffspring")])]});
            var Q4;
            Q4=makeQuery(id+"F7.opExtrude","SWEPT_BODY",BODY,{"disambiguationData":[OSD([sQuery(id+"F0.wireOp",EDGE,"E7"),sQuery(id+"F0.wireOp",EDGE,"E17"),sQuery(id+"F0.wireOp",EDGE,"E40.0"),sQuery(id+"F0.wireOp",EDGE,"E41.0"),sQuery(id+"F0.wireOp",EDGE,"E42.0"),sQuery(id+"F0.wireOp",EDGE,"E43.trimOffspring"),sQuery(id+"F0.wireOp",EDGE,"E44.trimOffspring"),sQuery(id+"F0.wireOp",EDGE,"E50")])]});
            var Q5;
            Q5=makeQuery(id+"F7.opExtrude","SWEPT_BODY",BODY,{"disambiguationData":[OSD([sQuery(id+"F0.wireOp",EDGE,"E5"),sQuery(id+"F0.wireOp",EDGE,"E25"),sQuery(id+"F0.wireOp",EDGE,"E56.0"),sQuery(id+"F0.wireOp",EDGE,"E56.1"),sQuery(id+"F0.wireOp",EDGE,"E57.0"),sQuery(id+"F0.wireOp",EDGE,"E58.0"),sQuery(id+"F0.wireOp",EDGE,"E59.trimOffspring"),sQuery(id+"F0.wireOp",EDGE,"E60.trimOffspring")])]});
            var Q6;
            Q6=makeQuery(id+"F1.opExtrude","SWEPT_BODY",BODY,{"disambiguationData":[OSD([sQuery(id+"F0.wireOp",EDGE,"E0.0"),sQuery(id+"F0.wireOp",EDGE,"E0.1"),sQuery(id+"F0.wireOp",EDGE,"E0.2"),sQuery(id+"F0.wireOp",EDGE,"E1.0"),sQuery(id+"F0.wireOp",EDGE,"E1.1"),sQuery(id+"F0.wireOp",EDGE,"E1.2"),sQuery(id+"F0.wireOp",EDGE,"E2"),sQuery(id+"F0.wireOp",EDGE,"E3"),sQuery(id+"F0.wireOp",EDGE,"E4"),sQuery(id+"F0.wireOp",EDGE,"E5"),sQuery(id+"F0.wireOp",EDGE,"E6"),sQuery(id+"F0.wireOp",EDGE,"E7"),sQuery(id+"F0.wireOp",EDGE,"E8"),sQuery(id+"F0.wireOp",EDGE,"E9"),sQuery(id+"F0.wireOp",EDGE,"E10"),sQuery(id+"F0.wireOp",EDGE,"E11"),sQuery(id+"F0.wireOp",EDGE,"E12"),sQuery(id+"F0.wireOp",EDGE,"E13"),sQuery(id+"F0.wireOp",EDGE,"E14.0"),sQuery(id+"F0.wireOp",EDGE,"E14.1"),sQuery(id+"F0.wireOp",EDGE,"E14.2"),sQuery(id+"F0.wireOp",EDGE,"E14.3"),sQuery(id+"F0.wireOp",EDGE,"E14.4"),sQuery(id+"F0.wireOp",EDGE,"E14.5"),sQuery(id+"F0.wireOp",EDGE,"E15"),sQuery(id+"F0.wireOp",EDGE,"E16"),sQuery(id+"F0.wireOp",EDGE,"E17"),sQuery(id+"F0.wireOp",EDGE,"E18"),sQuery(id+"F0.wireOp",EDGE,"E19"),sQuery(id+"F0.wireOp",EDGE,"E20"),sQuery(id+"F0.wireOp",EDGE,"E21"),sQuery(id+"F0.wireOp",EDGE,"E22"),sQuery(id+"F0.wireOp",EDGE,"E23"),sQuery(id+"F0.wireOp",EDGE,"E24"),sQuery(id+"F0.wireOp",EDGE,"E25"),sQuery(id+"F0.wireOp",EDGE,"E26"),sQuery(id+"F0.wireOp",EDGE,"E29.0"),sQuery(id+"F0.wireOp",EDGE,"E29.1"),sQuery(id+"F0.wireOp",EDGE,"E30.0"),sQuery(id+"F0.wireOp",EDGE,"E31.0"),sQuery(id+"F0.wireOp",EDGE,"E32.trimOffspring"),sQuery(id+"F0.wireOp",EDGE,"E34.trimOffspring"),sQuery(id+"F0.wireOp",EDGE,"E35.0"),sQuery(id+"F0.wireOp",EDGE,"E35.1"),sQuery(id+"F0.wireOp",EDGE,"E36.0"),sQuery(id+"F0.wireOp",EDGE,"E37.0"),sQuery(id+"F0.wireOp",EDGE,"E38.trimOffspring"),sQuery(id+"F0.wireOp",EDGE,"E39.trimOffspring"),sQuery(id+"F0.wireOp",EDGE,"E40.0"),sQuery(id+"F0.wireOp",EDGE,"E41.0"),sQuery(id+"F0.wireOp",EDGE,"E42.0"),sQuery(id+"F0.wireOp",EDGE,"E43.trimOffspring"),sQuery(id+"F0.wireOp",EDGE,"E44.trimOffspring"),sQuery(id+"F0.wireOp",EDGE,"E45.0"),sQuery(id+"F0.wireOp",EDGE,"E45.1"),sQuery(id+"F0.wireOp",EDGE,"E46.0"),sQuery(id+"F0.wireOp",EDGE,"E47.0"),sQuery(id+"F0.wireOp",EDGE,"E48.trimOffspring"),sQuery(id+"F0.wireOp",EDGE,"E49.trimOffspring"),sQuery(id+"F0.wireOp",EDGE,"E50"),sQuery(id+"F0.wireOp",EDGE,"E51.0"),sQuery(id+"F0.wireOp",EDGE,"E52.0"),sQuery(id+"F0.wireOp",EDGE,"E53.0"),sQuery(id+"F0.wireOp",EDGE,"E54.trimOffspring"),sQuery(id+"F0.wireOp",EDGE,"E55.trimOffspring"),sQuery(id+"F0.wireOp",EDGE,"E56.0"),sQuery(id+"F0.wireOp",EDGE,"E56.1"),sQuery(id+"F0.wireOp",EDGE,"E57.0"),sQuery(id+"F0.wireOp",EDGE,"E58.0"),sQuery(id+"F0.wireOp",EDGE,"E59.trimOffspring"),sQuery(id+"F0.wireOp",EDGE,"E60.trimOffspring"),sQuery(id+"F0.wireOp",EDGE,"E61")])]});
            var Q7;
            {var subQ0=sQuery(id+"F0.wireOp",EDGE,"E10");var subQ1=sQuery(id+"F0.wireOp",EDGE,"E0.2");Q7=makeQuery(id+"F4.opFillet","BLEND_VERTEX",VERTEX,{"blendedFrom":[makeQuery(id+"F1.opExtrude","CAP_VERTEX",VERTEX,{"disambiguationData":[OSD([subQ1,subQ0])],"isStart":false}),makeQuery(id+"F1.opExtrude","CAP_EDGE",EDGE,{"disambiguationData":[OSD([subQ1])],"isStart":false}),makeQuery(id+"F1.opExtrude","CAP_EDGE",EDGE,{"disambiguationData":[OSD([subQ0])],"isStart":false}),makeQuery(id+"F1.opExtrude","CAP_FACE",FACE,{"disambiguationData":[OSD([sQuery(id+"F0.wireOp",EDGE,"E0.0"),sQuery(id+"F0.wireOp",EDGE,"E0.1"),subQ1,sQuery(id+"F0.wireOp",EDGE,"E1.0"),sQuery(id+"F0.wireOp",EDGE,"E1.1"),sQuery(id+"F0.wireOp",EDGE,"E1.2"),sQuery(id+"F0.wireOp",EDGE,"E2"),sQuery(id+"F0.wireOp",EDGE,"E3"),sQuery(id+"F0.wireOp",EDGE,"E4"),sQuery(id+"F0.wireOp",EDGE,"E5"),sQuery(id+"F0.wireOp",EDGE,"E6"),sQuery(id+"F0.wireOp",EDGE,"E7"),sQuery(id+"F0.wireOp",EDGE,"E8"),sQuery(id+"F0.wireOp",EDGE,"E9"),subQ0,sQuery(id+"F0.wireOp",EDGE,"E11"),sQuery(id+"F0.wireOp",EDGE,"E12"),sQuery(id+"F0.wireOp",EDGE,"E13"),sQuery(id+"F0.wireOp",EDGE,"E14.0"),sQuery(id+"F0.wireOp",EDGE,"E14.1"),sQuery(id+"F0.wireOp",EDGE,"E14.2"),sQuery(id+"F0.wireOp",EDGE,"E14.3"),sQuery(id+"F0.wireOp",EDGE,"E14.4"),sQuery(id+"F0.wireOp",EDGE,"E14.5"),sQuery(id+"F0.wireOp",EDGE,"E15"),sQuery(id+"F0.wireOp",EDGE,"E16"),sQuery(id+"F0.wireOp",EDGE,"E17"),sQuery(id+"F0.wireOp",EDGE,"E18"),sQuery(id+"F0.wireOp",EDGE,"E19"),sQuery(id+"F0.wireOp",EDGE,"E20"),sQuery(id+"F0.wireOp",EDGE,"E21"),sQuery(id+"F0.wireOp",EDGE,"E22"),sQuery(id+"F0.wireOp",EDGE,"E23"),sQuery(id+"F0.wireOp",EDGE,"E24"),sQuery(id+"F0.wireOp",EDGE,"E25"),sQuery(id+"F0.wireOp",EDGE,"E26"),sQuery(id+"F0.wireOp",EDGE,"E29.0"),sQuery(id+"F0.wireOp",EDGE,"E29.1"),sQuery(id+"F0.wireOp",EDGE,"E30.0"),sQuery(id+"F0.wireOp",EDGE,"E31.0"),sQuery(id+"F0.wireOp",EDGE,"E32.trimOffspring"),sQuery(id+"F0.wireOp",EDGE,"E34.trimOffspring"),sQuery(id+"F0.wireOp",EDGE,"E35.0"),sQuery(id+"F0.wireOp",EDGE,"E35.1"),sQuery(id+"F0.wireOp",EDGE,"E36.0"),sQuery(id+"F0.wireOp",EDGE,"E37.0"),sQuery(id+"F0.wireOp",EDGE,"E38.trimOffspring"),sQuery(id+"F0.wireOp",EDGE,"E39.trimOffspring"),sQuery(id+"F0.wireOp",EDGE,"E40.0"),sQuery(id+"F0.wireOp",EDGE,"E41.0"),sQuery(id+"F0.wireOp",EDGE,"E42.0"),sQuery(id+"F0.wireOp",EDGE,"E43.trimOffspring"),sQuery(id+"F0.wireOp",EDGE,"E44.trimOffspring"),sQuery(id+"F0.wireOp",EDGE,"E45.0"),sQuery(id+"F0.wireOp",EDGE,"E45.1"),sQuery(id+"F0.wireOp",EDGE,"E46.0"),sQuery(id+"F0.wireOp",EDGE,"E47.0"),sQuery(id+"F0.wireOp",EDGE,"E48.trimOffspring"),sQuery(id+"F0.wireOp",EDGE,"E49.trimOffspring"),sQuery(id+"F0.wireOp",EDGE,"E50"),sQuery(id+"F0.wireOp",EDGE,"E51.0"),sQuery(id+"F0.wireOp",EDGE,"E52.0"),sQuery(id+"F0.wireOp",EDGE,"E53.0"),sQuery(id+"F0.wireOp",EDGE,"E54.trimOffspring"),sQuery(id+"F0.wireOp",EDGE,"E55.trimOffspring"),sQuery(id+"F0.wireOp",EDGE,"E56.0"),sQuery(id+"F0.wireOp",EDGE,"E56.1"),sQuery(id+"F0.wireOp",EDGE,"E57.0"),sQuery(id+"F0.wireOp",EDGE,"E58.0"),sQuery(id+"F0.wireOp",EDGE,"E59.trimOffspring"),sQuery(id+"F0.wireOp",EDGE,"E60.trimOffspring"),sQuery(id+"F0.wireOp",EDGE,"E61")])],"isStart":false})],"blendedInto":[makeQuery(id+"F1.opExtrude","CAP_FACE",FACE,{"disambiguationData":[OSD([sQuery(id+"F0.wireOp",EDGE,"E0.0"),sQuery(id+"F0.wireOp",EDGE,"E0.1"),subQ1,sQuery(id+"F0.wireOp",EDGE,"E1.0"),sQuery(id+"F0.wireOp",EDGE,"E1.1"),sQuery(id+"F0.wireOp",EDGE,"E1.2"),sQuery(id+"F0.wireOp",EDGE,"E2"),sQuery(id+"F0.wireOp",EDGE,"E3"),sQuery(id+"F0.wireOp",EDGE,"E4"),sQuery(id+"F0.wireOp",EDGE,"E5"),sQuery(id+"F0.wireOp",EDGE,"E6"),sQuery(id+"F0.wireOp",EDGE,"E7"),sQuery(id+"F0.wireOp",EDGE,"E8"),sQuery(id+"F0.wireOp",EDGE,"E9"),subQ0,sQuery(id+"F0.wireOp",EDGE,"E11"),sQuery(id+"F0.wireOp",EDGE,"E12"),sQuery(id+"F0.wireOp",EDGE,"E13"),sQuery(id+"F0.wireOp",EDGE,"E14.0"),sQuery(id+"F0.wireOp",EDGE,"E14.1"),sQuery(id+"F0.wireOp",EDGE,"E14.2"),sQuery(id+"F0.wireOp",EDGE,"E14.3"),sQuery(id+"F0.wireOp",EDGE,"E14.4"),sQuery(id+"F0.wireOp",EDGE,"E14.5"),sQuery(id+"F0.wireOp",EDGE,"E15"),sQuery(id+"F0.wireOp",EDGE,"E16"),sQuery(id+"F0.wireOp",EDGE,"E17"),sQuery(id+"F0.wireOp",EDGE,"E18"),sQuery(id+"F0.wireOp",EDGE,"E19"),sQuery(id+"F0.wireOp",EDGE,"E20"),sQuery(id+"F0.wireOp",EDGE,"E21"),sQuery(id+"F0.wireOp",EDGE,"E22"),sQuery(id+"F0.wireOp",EDGE,"E23"),sQuery(id+"F0.wireOp",EDGE,"E24"),sQuery(id+"F0.wireOp",EDGE,"E25"),sQuery(id+"F0.wireOp",EDGE,"E26"),sQuery(id+"F0.wireOp",EDGE,"E29.0"),sQuery(id+"F0.wireOp",EDGE,"E29.1"),sQuery(id+"F0.wireOp",EDGE,"E30.0"),sQuery(id+"F0.wireOp",EDGE,"E31.0"),sQuery(id+"F0.wireOp",EDGE,"E32.trimOffspring"),sQuery(id+"F0.wireOp",EDGE,"E34.trimOffspring"),sQuery(id+"F0.wireOp",EDGE,"E35.0"),sQuery(id+"F0.wireOp",EDGE,"E35.1"),sQuery(id+"F0.wireOp",EDGE,"E36.0"),sQuery(id+"F0.wireOp",EDGE,"E37.0"),sQuery(id+"F0.wireOp",EDGE,"E38.trimOffspring"),sQuery(id+"F0.wireOp",EDGE,"E39.trimOffspring"),sQuery(id+"F0.wireOp",EDGE,"E40.0"),sQuery(id+"F0.wireOp",EDGE,"E41.0"),sQuery(id+"F0.wireOp",EDGE,"E42.0"),sQuery(id+"F0.wireOp",EDGE,"E43.trimOffspring"),sQuery(id+"F0.wireOp",EDGE,"E44.trimOffspring"),sQuery(id+"F0.wireOp",EDGE,"E45.0"),sQuery(id+"F0.wireOp",EDGE,"E45.1"),sQuery(id+"F0.wireOp",EDGE,"E46.0"),sQuery(id+"F0.wireOp",EDGE,"E47.0"),sQuery(id+"F0.wireOp",EDGE,"E48.trimOffspring"),sQuery(id+"F0.wireOp",EDGE,"E49.trimOffspring"),sQuery(id+"F0.wireOp",EDGE,"E50"),sQuery(id+"F0.wireOp",EDGE,"E51.0"),sQuery(id+"F0.wireOp",EDGE,"E52.0"),sQuery(id+"F0.wireOp",EDGE,"E53.0"),sQuery(id+"F0.wireOp",EDGE,"E54.trimOffspring"),sQuery(id+"F0.wireOp",EDGE,"E55.trimOffspring"),sQuery(id+"F0.wireOp",EDGE,"E56.0"),sQuery(id+"F0.wireOp",EDGE,"E56.1"),sQuery(id+"F0.wireOp",EDGE,"E57.0"),sQuery(id+"F0.wireOp",EDGE,"E58.0"),sQuery(id+"F0.wireOp",EDGE,"E59.trimOffspring"),sQuery(id+"F0.wireOp",EDGE,"E60.trimOffspring"),sQuery(id+"F0.wireOp",EDGE,"E61")])],"isStart":false})]});}
            var Q8;
            Q8=makeQuery(id+"F1.opExtrude","CAP_VERTEX",VERTEX,{"disambiguationData":[OSD([sQuery(id+"F0.wireOp",EDGE,"E51.0"),sQuery(id+"F0.wireOp",EDGE,"E54.trimOffspring")])],"isStart":false});
            transform(context, id + "F11", {"entities" : qUnion([Q0, Q1, Q2, Q3, Q4, Q5, Q6]), "transformType" : TransformType.SCALE_UNIFORMLY, "scale" : .8, "scalePoint" : qUnion([Q8]), "makeCopy" : false});
        }
    });
